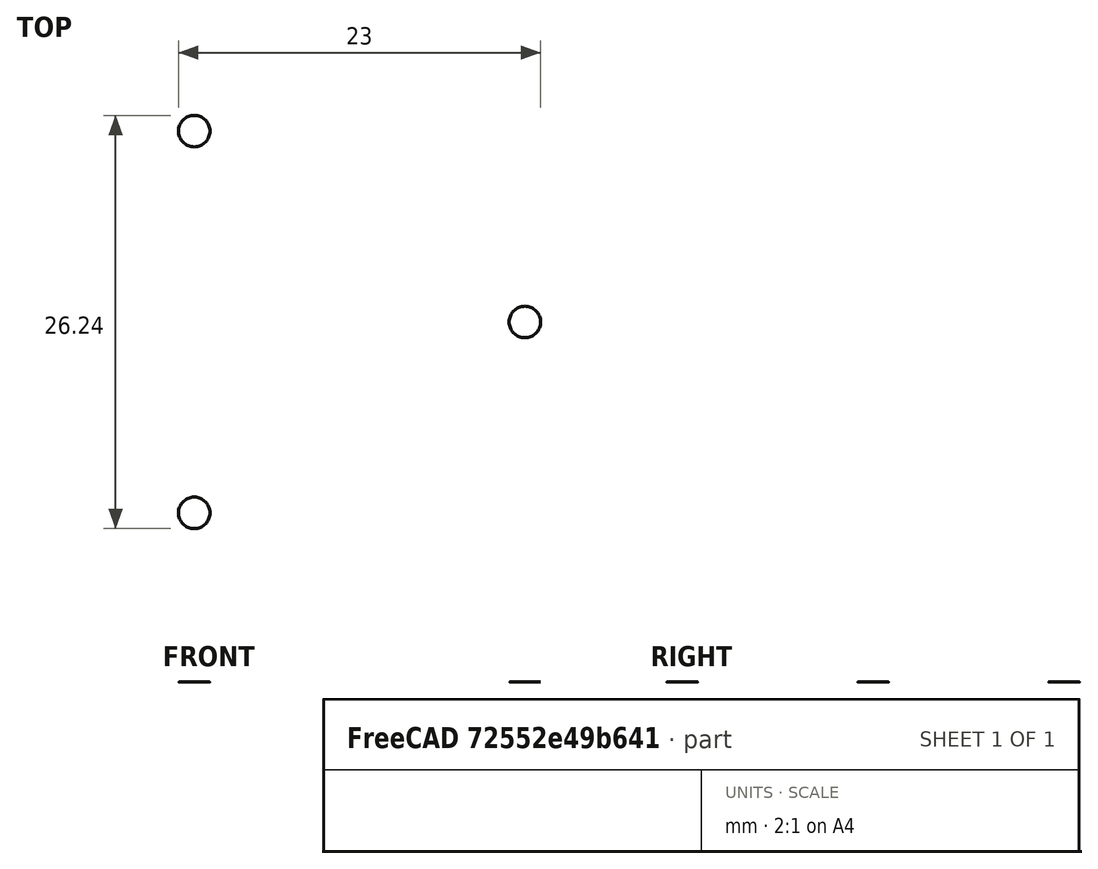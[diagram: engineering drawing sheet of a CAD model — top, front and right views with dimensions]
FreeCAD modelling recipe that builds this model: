
FCSTD DOCUMENT  (FreeCAD 0.16RUnknown)
Label: mass
License: All rights reserved
LicenseURL: http://en.wikipedia.org/wiki/All_rights_reserved
objects: Part::Part2DObjectPython×2, Part::FeaturePython×1, Spreadsheet::Sheet×1
note: 3 computed .brp shape members not serialized (recipe doc carries the construction recipe); baked Part::Feature solids carry a one-line shape summary decoded from their .brp

FEATURE [Part::Part2DObjectPython] Polygon  label="triangle"  # Draft 2D object (typed FeaturePython)
  ChamferSize = 0
  DrawMode = 0
  FacesNumber = 3
  FilletRadius = 2.5
  MakeFace = true
  Radius = 20
  expr: Radius = Spreadsheet.baseRad
  expr: FacesNumber = Spreadsheet.faceNum
FEATURE [Part::Part2DObjectPython] Circle  # Draft 2D object (typed FeaturePython)
  FirstAngle = 0
  LastAngle = 0
  MakeFace = true
  Placement = pos=(14,0,0) rot=(0,0,1;0rad)
  Radius = 1
  expr: Placement.Base.x = Spreadsheet.baseRad - 6
FEATURE [Part::FeaturePython] Array  # Draft array (typed FeaturePython)
  Angle = 360
  ArrayType = 1
  Axis = (0,0,1)
  Base = -> Circle
  Center = (0,0,0)
  Fuse = false
  IntervalAxis = (0,0,0)
  IntervalX = (1,0,0)
  IntervalY = (0,1,0)
  IntervalZ = (0,0,0)
  NumberPolar = 3
  NumberX = 1
  NumberY = 1
  NumberZ = 1
  expr: NumberPolar = Spreadsheet.faceNum
FEATURE [Spreadsheet::Sheet] Spreadsheet
  cells = A1=base radius; B1(baseRad)=20; C1=mm; D1=name = baseRad; A2=face number; B2(faceNum)=3; C2=faces; D2=name = faceNum
